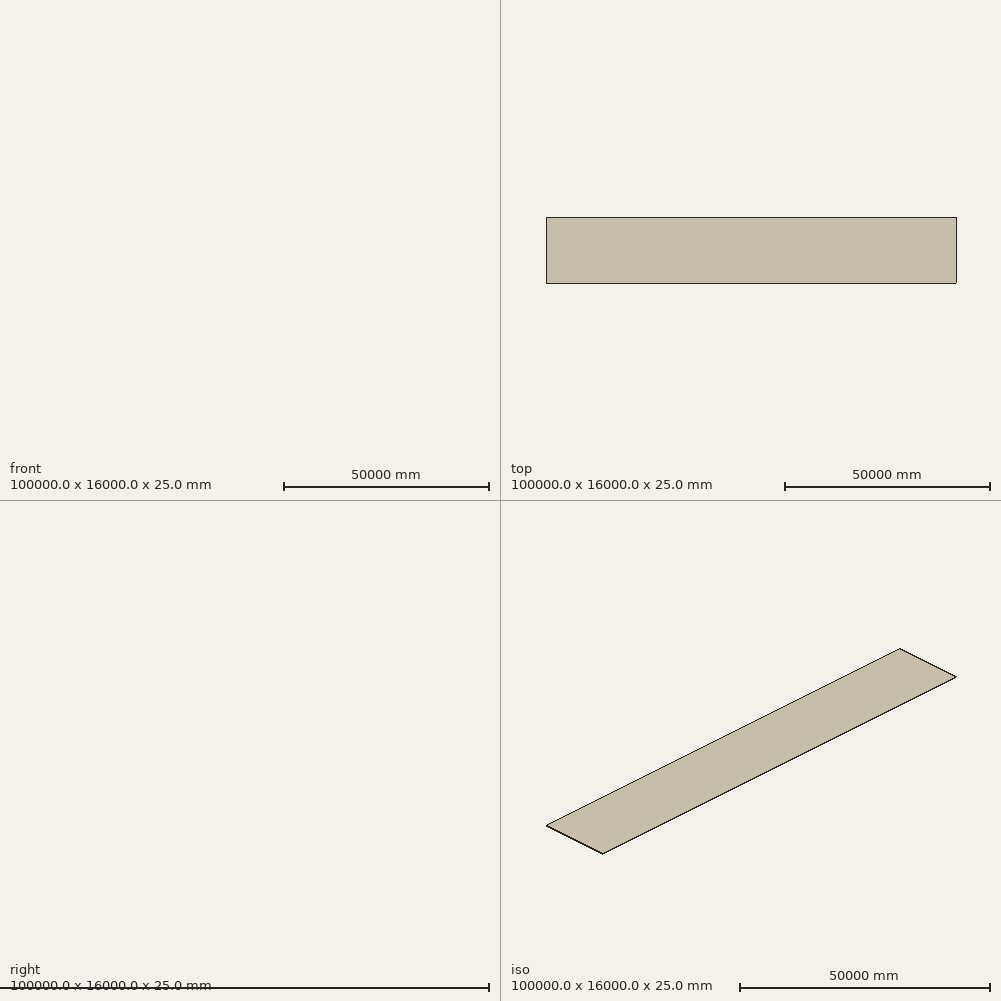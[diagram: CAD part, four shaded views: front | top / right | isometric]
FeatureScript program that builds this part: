
annotation { "Feature Type Name" : "Feature", "Feature Type Description" : "" }
export const myFeature = defineFeature(function(context is Context, id is Id, definition is map)
    precondition{}
    {
        {
            var Q0;
            Q0=qCreatedBy(makeId("Top.planeOp"),FACE);
            var sketch = newSketch(context, id + "F0", { "sketchPlane" : qUnion([Q0])});
            skLineSegment(sketch, "E0.bottom", {"start": v(-50000, 8000) * mm, "end": v(50000, 8000) * mm});
            skLineSegment(sketch, "E0.top", {"start": v(-50000, -8000) * mm, "end": v(50000, -8000) * mm});
            skLineSegment(sketch, "E0.left", {"start": v(-50000, 8000) * mm, "end": v(-50000, -8000) * mm});
            skLineSegment(sketch, "E0.right", {"start": v(50000, 8000) * mm, "end": v(50000, -8000) * mm});
            skPoint(sketch, "E0.middle", {"position": v(0, 0) * mm});
            skSolve(sketch);
        }
        {
            var Q0;
            Q0 = qSketchRegion(id + "F0", true);
            extrude(context, id + "F1", {"entities" : qUnion([Q0]), "depth" : 25 * mm, "offsetDistance" : 25 * mm});
        }
    });
